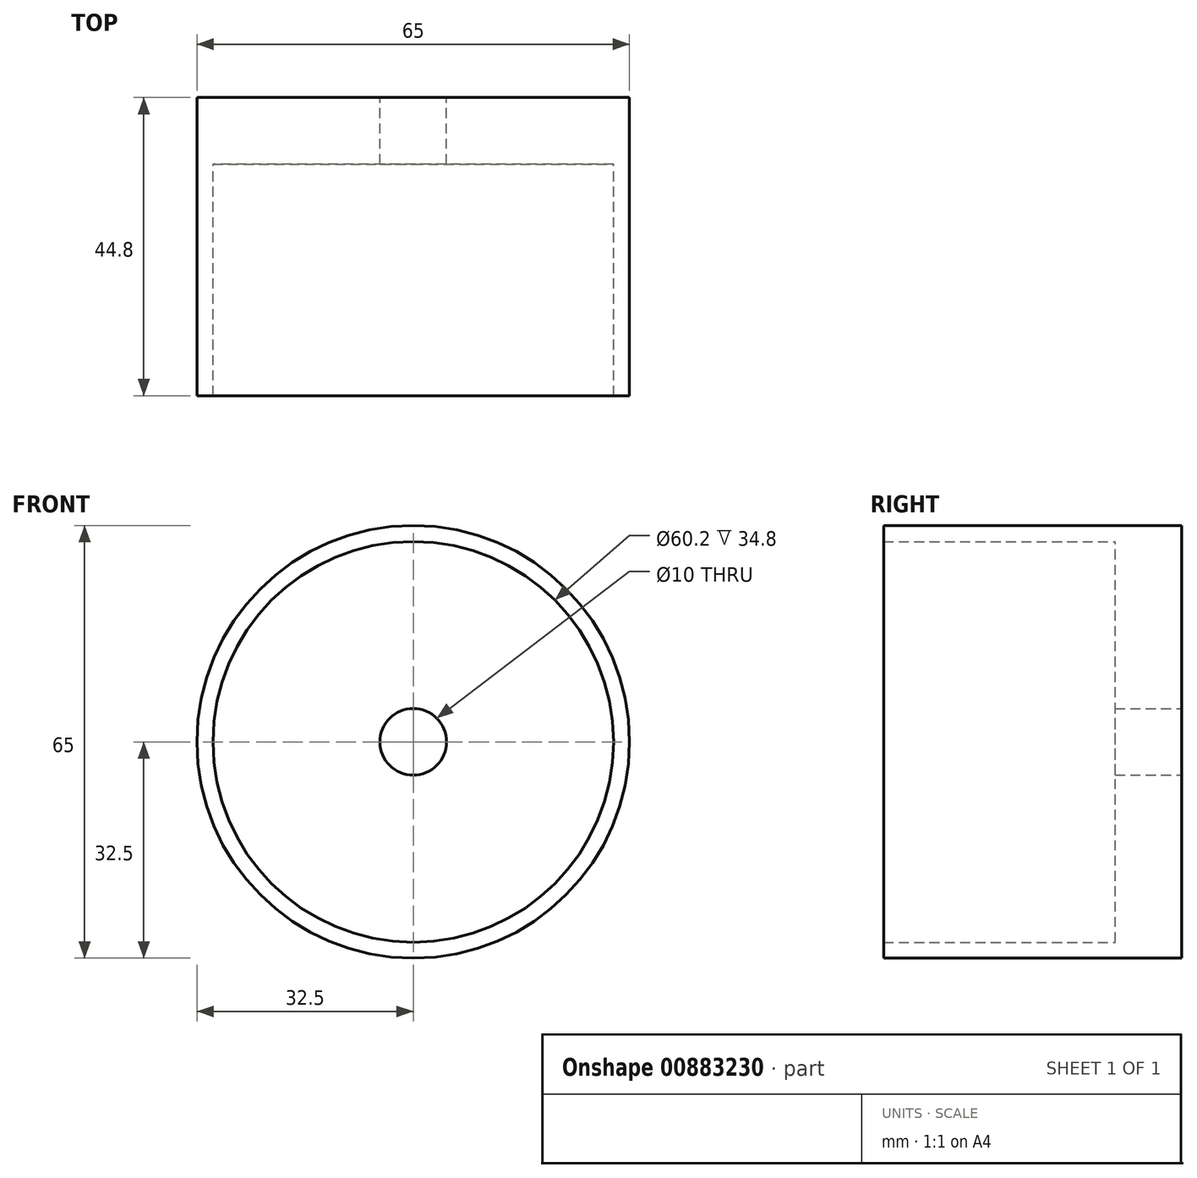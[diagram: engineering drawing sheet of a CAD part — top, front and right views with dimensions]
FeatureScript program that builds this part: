
annotation { "Feature Type Name" : "Feature", "Feature Type Description" : "" }
export const myFeature = defineFeature(function(context is Context, id is Id, definition is map)
    precondition{}
    {
        {
            var Q0;
            Q0=qCreatedBy(makeId("Front.planeOp"),FACE);
            var sketch = newSketch(context, id + "F0", { "sketchPlane" : qUnion([Q0])});
            skCircle(sketch, "E0", {"center": v(0, 0) * mm, "radius": 30.1 * mm});
            skCircle(sketch, "E1", {"center": v(0, 0) * mm, "radius": 32.5 * mm});
            skSolve(sketch);
        }
        {
            var Q0;
            Q0 = qSketchRegion(id + "F0", true);
            extrude(context, id + "F1", {"entities" : qUnion([Q0]), "depth" : 44.8 * mm, "offsetDistance" : 25 * mm});
        }
        {
            var Q0;
            Q0=qCreatedBy(makeId("Front.planeOp"),FACE);
            var sketch = newSketch(context, id + "F2", { "sketchPlane" : qUnion([Q0])});
            skCircle(sketch, "E2", {"center": v(0, 0) * mm, "radius": 30.1 * mm});
            skCircle(sketch, "E3", {"center": v(0, 0) * mm, "radius": 5 * mm});
            skSolve(sketch);
        }
        {
            var Q0;
            Q0 = qSketchRegion(id + "F2", true);
            extrude(context, id + "F3", {"entities" : qUnion([Q0]), "operationType" : NewBodyOperationType.ADD, "depth" : 10 * mm, "offsetDistance" : 25 * mm});
        }
    });
